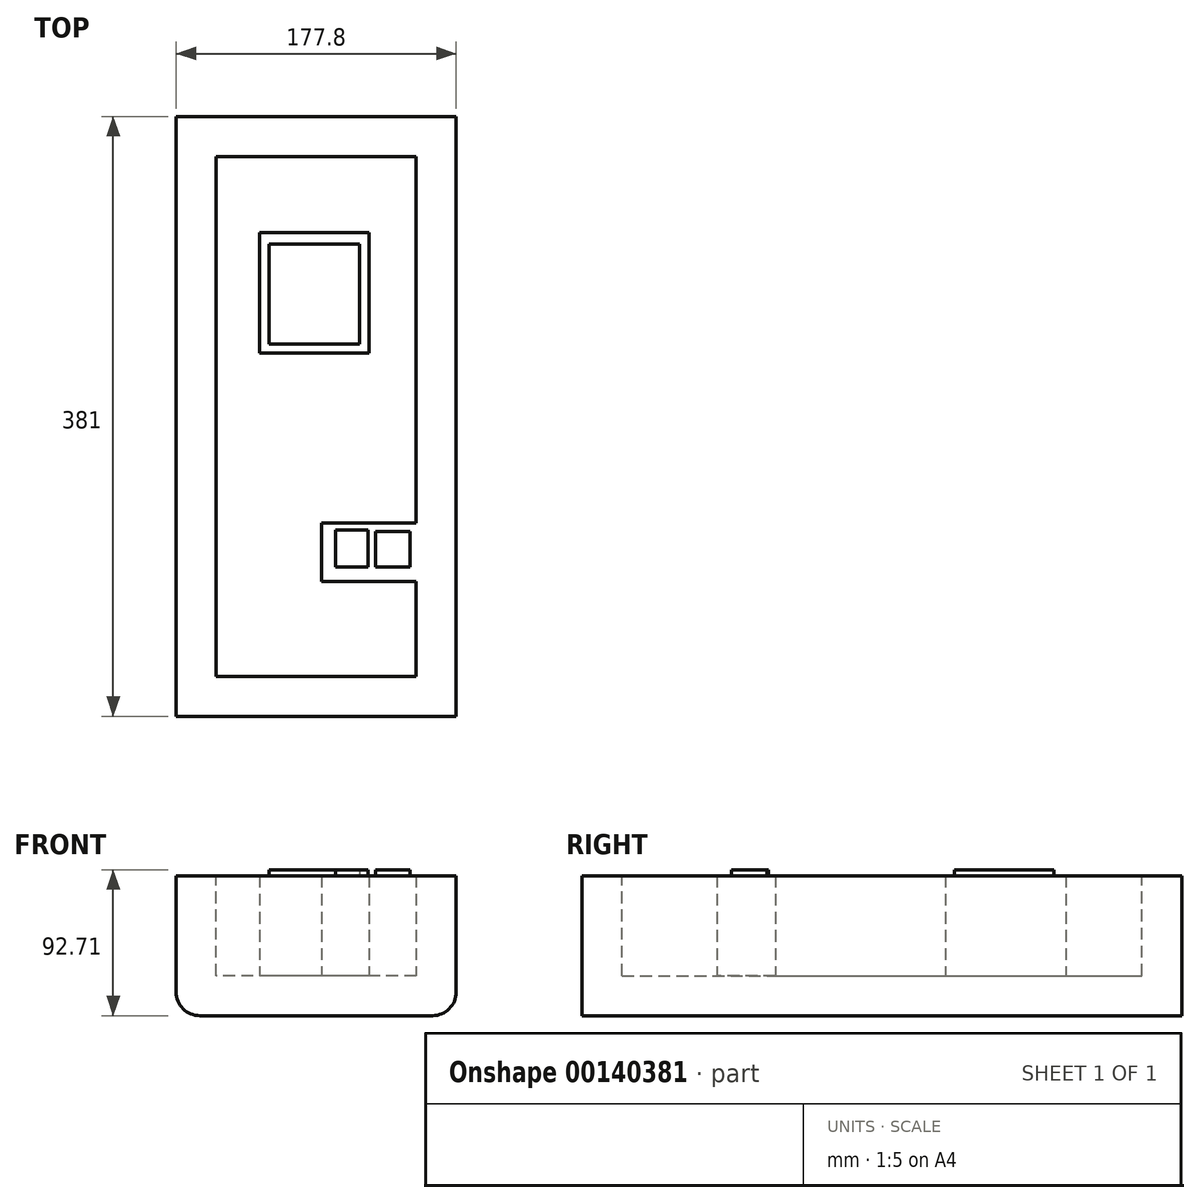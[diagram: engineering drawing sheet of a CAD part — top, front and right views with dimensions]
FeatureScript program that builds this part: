
annotation { "Feature Type Name" : "Feature", "Feature Type Description" : "" }
export const myFeature = defineFeature(function(context is Context, id is Id, definition is map)
    precondition{}
    {
        {
            var Q0;
            Q0=qCreatedBy(makeId("Front.planeOp"),FACE);
            var sketch = newSketch(context, id + "F0", { "sketchPlane" : qUnion([Q0])});
            skLineSegment(sketch, "E0.bottom", {"start": v(90.1, -44.45) * mm, "end": v(-87.7, -44.45) * mm});
            skLineSegment(sketch, "E0.top", {"start": v(90.1, 44.45) * mm, "end": v(-87.7, 44.45) * mm});
            skLineSegment(sketch, "E0.left", {"start": v(90.1, -44.45) * mm, "end": v(90.1, 44.45) * mm});
            skLineSegment(sketch, "E0.right", {"start": v(-87.7, -44.45) * mm, "end": v(-87.7, 44.45) * mm});
            skPoint(sketch, "E0.middle", {"position": v(1.2, 0) * mm});
            skSolve(sketch);
        }
        {
            var Q0;
            Q0 = qSketchRegion(id + "F0", true);
            var Q1;
            Q1=makeQuery(id+"F0.imprint","IMPRINT",FACE,{"disambiguationData":[TD([[makeQuery(id+"F0.imprint","IMPRINT",EDGE,{"derivedFrom":sQuery(id+"F0.wireOp",EDGE,"E0.bottom")}),-1.0]])]});
            extrude(context, id + "F1", {"entities" : qUnion([Q0, Q1]), "depth" : 381 * mm});
        }
        {
            var Q0;
            Q0=makeQuery(id+"F1.opExtrude","SWEPT_FACE",FACE,{"disambiguationData":[OSD([sQuery(id+"F0.wireOp",EDGE,"E0.top")])]});
            shell(context, id + "F2", {"entities" : qUnion([Q0]), "thickness" : 25.4 * mm});
        }
        {
            var Q0;
            Q0=makeQuery(id+"F2.opShell","OFFSET_FACE",FACE,{"disambiguationData":[OSD([sQuery(id+"F0.wireOp",EDGE,"E0.bottom")])]});
            var sketch = newSketch(context, id + "F3", { "sketchPlane" : qUnion([Q0])});
            skLineSegment(sketch, "E1.bottom", {"start": v(34.64, -150.36) * mm, "end": v(-34.64, -150.36) * mm});
            skLineSegment(sketch, "E1.top", {"start": v(34.64, -73.83) * mm, "end": v(-34.64, -73.83) * mm});
            skLineSegment(sketch, "E1.left", {"start": v(34.64, -150.36) * mm, "end": v(34.64, -73.83) * mm});
            skLineSegment(sketch, "E1.right", {"start": v(-34.64, -150.36) * mm, "end": v(-34.64, -73.83) * mm});
            skPoint(sketch, "E1.middle", {"position": v(0, -112.1) * mm});
            skLineSegment(sketch, "E2.bottom", {"start": v(64.7, -258.17) * mm, "end": v(4.59, -258.17) * mm});
            skLineSegment(sketch, "E2.top", {"start": v(64.7, -295.5) * mm, "end": v(4.59, -295.5) * mm});
            skLineSegment(sketch, "E2.left", {"start": v(64.7, -258.17) * mm, "end": v(64.7, -295.5) * mm});
            skLineSegment(sketch, "E2.right", {"start": v(4.59, -258.17) * mm, "end": v(4.59, -295.5) * mm});
            skPoint(sketch, "E2.middle", {"position": v(34.64, -276.83) * mm});
            skSolve(sketch);
        }
        {
            var Q0;
            Q0 = qSketchRegion(id + "F3", true);
            extrude(context, id + "F4", {"entities" : qUnion([Q0]), "operationType" : NewBodyOperationType.ADD, "depth" : 63.5 * mm});
        }
        {
            var Q0;
            Q0=makeQuery(id+"F4.opExtrude","CAP_FACE",FACE,{"disambiguationData":[OSD([sQuery(id+"F3.wireOp",EDGE,"E1.bottom"),sQuery(id+"F3.wireOp",EDGE,"E1.top"),sQuery(id+"F3.wireOp",EDGE,"E1.left"),sQuery(id+"F3.wireOp",EDGE,"E1.right")])],"isStart":false});
            var sketch = newSketch(context, id + "F5", { "sketchPlane" : qUnion([Q0])});
            skLineSegment(sketch, "E3.bottom", {"start": v(28.72, -81.27) * mm, "end": v(-28.72, -81.27) * mm});
            skLineSegment(sketch, "E3.top", {"start": v(28.72, -144.66) * mm, "end": v(-28.72, -144.66) * mm});
            skLineSegment(sketch, "E3.left", {"start": v(28.72, -81.27) * mm, "end": v(28.72, -144.66) * mm});
            skLineSegment(sketch, "E3.right", {"start": v(-28.72, -81.27) * mm, "end": v(-28.72, -144.66) * mm});
            skPoint(sketch, "E3.middle", {"position": v(0, -112.96) * mm});
            skLineSegment(sketch, "E4.bottom", {"start": v(60.9, -286.14) * mm, "end": v(38.78, -286.14) * mm});
            skLineSegment(sketch, "E4.top", {"start": v(60.9, -263.59) * mm, "end": v(38.78, -263.59) * mm});
            skLineSegment(sketch, "E4.left", {"start": v(60.9, -286.14) * mm, "end": v(60.9, -263.59) * mm});
            skLineSegment(sketch, "E4.right", {"start": v(38.78, -286.14) * mm, "end": v(38.78, -263.59) * mm});
            skPoint(sketch, "E4.middle", {"position": v(49.84, -274.86) * mm});
            skLineSegment(sketch, "E5.bottom", {"start": v(34.08, -286.14) * mm, "end": v(13.41, -286.14) * mm});
            skLineSegment(sketch, "E5.top", {"start": v(34.08, -262.7) * mm, "end": v(13.41, -262.7) * mm});
            skLineSegment(sketch, "E5.left", {"start": v(34.08, -286.14) * mm, "end": v(34.08, -262.7) * mm});
            skLineSegment(sketch, "E5.right", {"start": v(13.41, -286.14) * mm, "end": v(13.41, -262.7) * mm});
            skPoint(sketch, "E5.middle", {"position": v(23.74, -274.42) * mm});
            skPoint(sketch, "E5.cornerSnap0", {"position": v(49.84, -286.14) * mm});
            skSolve(sketch);
        }
        {
            var Q0;
            Q0 = qSketchRegion(id + "F5", true);
            extrude(context, id + "F6", {"entities" : qUnion([Q0]), "operationType" : NewBodyOperationType.ADD, "depth" : 3.8 * mm});
        }
        {
            var Q0;
            Q0=makeQuery(id+"F1.opExtrude","SWEPT_EDGE",EDGE,{"disambiguationData":[OSD([sQuery(id+"F0.wireOp",EDGE,"E0.bottom"),sQuery(id+"F0.wireOp",EDGE,"E0.left")])]});
            fillet(context, id + "F7", {"entities" : qUnion([Q0]), "radius" : 15 * mm, "tangentPropagation" : true, "allowEdgeOverflow" : false});
        }
        {
            var Q0;
            Q0=makeQuery(id+"F1.opExtrude","SWEPT_EDGE",EDGE,{"disambiguationData":[OSD([sQuery(id+"F0.wireOp",EDGE,"E0.bottom"),sQuery(id+"F0.wireOp",EDGE,"E0.right")])]});
            fillet(context, id + "F8", {"entities" : qUnion([Q0]), "radius" : 15 * mm, "tangentPropagation" : true, "allowEdgeOverflow" : false});
        }
    });
